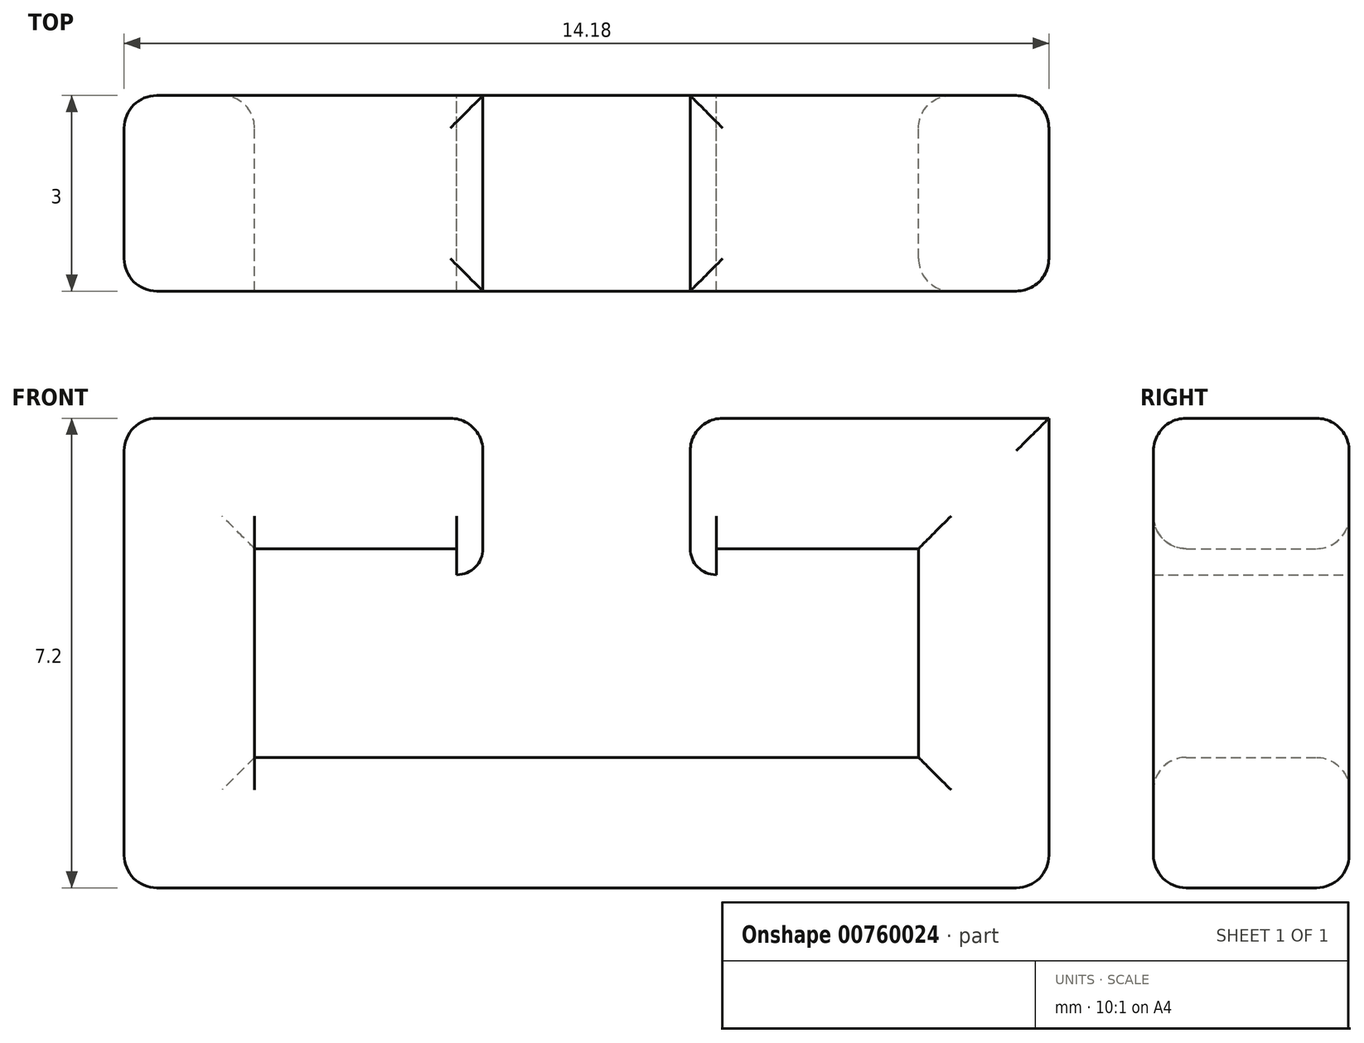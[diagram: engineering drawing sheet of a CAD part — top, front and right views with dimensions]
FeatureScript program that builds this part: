
annotation { "Feature Type Name" : "Feature", "Feature Type Description" : "" }
export const myFeature = defineFeature(function(context is Context, id is Id, definition is map)
    precondition{}
    {
        {
            var Q0;
            Q0=qCreatedBy(makeId("Front.planeOp"),FACE);
            var sketch = newSketch(context, id + "F0", { "sketchPlane" : qUnion([Q0])});
            skLineSegment(sketch, "E0.bottom", {"start": v(-7.09, -3.6) * mm, "end": v(7.09, -3.6) * mm});
            skLineSegment(sketch, "E0.top", {"start": v(-7.09, 3.6) * mm, "end": v(-1.59, 3.6) * mm});
            skLineSegment(sketch, "E0.left", {"start": v(-7.09, -3.6) * mm, "end": v(-7.09, 3.6) * mm});
            skLineSegment(sketch, "E0.right", {"start": v(7.09, -3.6) * mm, "end": v(7.09, 3.6) * mm});
            skPoint(sketch, "E0.middle", {"position": v(0, 0) * mm});
            skLineSegment(sketch, "E1.bottom", {"start": v(5.09, 1.6) * mm, "end": v(1.99, 1.6) * mm});
            skLineSegment(sketch, "E1.top", {"start": v(5.09, -1.6) * mm, "end": v(-5.09, -1.6) * mm});
            skLineSegment(sketch, "E1.left", {"start": v(5.09, 1.6) * mm, "end": v(5.09, -1.6) * mm});
            skLineSegment(sketch, "E1.right", {"start": v(-5.09, 1.6) * mm, "end": v(-5.09, -1.6) * mm});
            skLineSegment(sketch, "E2.top", {"start": v(1.59, 1.2) * mm, "end": v(1.99, 1.2) * mm});
            skLineSegment(sketch, "E2.left", {"start": v(1.59, 1.6) * mm, "end": v(1.59, 1.2) * mm});
            skLineSegment(sketch, "E2.right", {"start": v(1.99, 1.6) * mm, "end": v(1.99, 1.2) * mm});
            skLineSegment(sketch, "E3", {"start": v(-1.59, 1.6) * mm, "end": v(-1.59, 3.6) * mm});
            skLineSegment(sketch, "E4", {"start": v(1.59, 1.6) * mm, "end": v(1.59, 3.6) * mm});
            skLineSegment(sketch, "E5.trimOffspring", {"start": v(1.59, 3.6) * mm, "end": v(7.09, 3.6) * mm});
            skLineSegment(sketch, "E6.trimOffspring", {"start": v(-1.99, 1.6) * mm, "end": v(-5.09, 1.6) * mm});
            skLineSegment(sketch, "E7.top", {"start": v(-1.59, 1.2) * mm, "end": v(-1.99, 1.2) * mm});
            skLineSegment(sketch, "E7.left", {"start": v(-1.59, 1.6) * mm, "end": v(-1.59, 1.2) * mm});
            skLineSegment(sketch, "E7.right", {"start": v(-1.99, 1.6) * mm, "end": v(-1.99, 1.2) * mm});
            skSolve(sketch);
        }
        {
            var Q0;
            Q0=makeQuery(id+"F0.imprint","IMPRINT",FACE,{"disambiguationData":[TD([[makeQuery(id+"F0.imprint","IMPRINT",EDGE,{"derivedFrom":sQuery(id+"F0.wireOp",EDGE,"E0.bottom")}),1.0]])]});
            extrude(context, id + "F1", {"entities" : qUnion([Q0]), "depth" : 3 * mm, "offsetDistance" : 25 * mm});
        }
        {
            var Q0;
            Q0=makeQuery(id+"F1.opExtrude","CAP_EDGE",EDGE,{"disambiguationData":[OSD([sQuery(id+"F0.wireOp",EDGE,"E5.trimOffspring")])],"isStart":true});
            var Q1;
            Q1=makeQuery(id+"F1.opExtrude","CAP_EDGE",EDGE,{"disambiguationData":[OSD([sQuery(id+"F0.wireOp",EDGE,"E0.top")])],"isStart":true});
            var Q2;
            Q2=makeQuery(id+"F1.opExtrude","CAP_EDGE",EDGE,{"disambiguationData":[OSD([sQuery(id+"F0.wireOp",EDGE,"E0.left")])],"isStart":true});
            var Q3;
            Q3=makeQuery(id+"F1.opExtrude","CAP_EDGE",EDGE,{"disambiguationData":[OSD([sQuery(id+"F0.wireOp",EDGE,"E0.bottom")])],"isStart":true});
            var Q4;
            Q4=makeQuery(id+"F1.opExtrude","CAP_EDGE",EDGE,{"disambiguationData":[OSD([sQuery(id+"F0.wireOp",EDGE,"E0.right")])],"isStart":true});
            var Q5;
            Q5=makeQuery(id+"F1.opExtrude","SWEPT_EDGE",EDGE,{"disambiguationData":[OSD([sQuery(id+"F0.wireOp",EDGE,"E4"),sQuery(id+"F0.wireOp",EDGE,"E5.trimOffspring")])]});
            var Q6;
            Q6=makeQuery(id+"F1.opExtrude","SWEPT_EDGE",EDGE,{"disambiguationData":[OSD([sQuery(id+"F0.wireOp",EDGE,"E0.top"),sQuery(id+"F0.wireOp",EDGE,"E3")])]});
            var Q7;
            Q7=makeQuery(id+"F1.opExtrude","CAP_EDGE",EDGE,{"disambiguationData":[OSD([sQuery(id+"F0.wireOp",EDGE,"E0.top")])],"isStart":false});
            var Q8;
            Q8=makeQuery(id+"F1.opExtrude","SWEPT_EDGE",EDGE,{"disambiguationData":[OSD([sQuery(id+"F0.wireOp",EDGE,"E0.top"),sQuery(id+"F0.wireOp",EDGE,"E0.left")])]});
            var Q9;
            Q9=makeQuery(id+"F1.opExtrude","CAP_EDGE",EDGE,{"disambiguationData":[OSD([sQuery(id+"F0.wireOp",EDGE,"E5.trimOffspring")])],"isStart":false});
            var Q10;
            Q10=makeQuery(id+"F1.opExtrude","CAP_EDGE",EDGE,{"disambiguationData":[OSD([sQuery(id+"F0.wireOp",EDGE,"E1.bottom")])],"isStart":false});
            var Q11;
            Q11=makeQuery(id+"F1.opExtrude","CAP_EDGE",EDGE,{"disambiguationData":[OSD([sQuery(id+"F0.wireOp",EDGE,"E6.trimOffspring")])],"isStart":false});
            var Q12;
            Q12=makeQuery(id+"F1.opExtrude","CAP_EDGE",EDGE,{"disambiguationData":[OSD([sQuery(id+"F0.wireOp",EDGE,"E1.bottom")])],"isStart":true});
            var Q13;
            Q13=makeQuery(id+"F1.opExtrude","CAP_EDGE",EDGE,{"disambiguationData":[OSD([sQuery(id+"F0.wireOp",EDGE,"E6.trimOffspring")])],"isStart":true});
            var Q14;
            Q14=makeQuery(id+"F1.opExtrude","CAP_EDGE",EDGE,{"disambiguationData":[OSD([sQuery(id+"F0.wireOp",EDGE,"E0.left")])],"isStart":false});
            var Q15;
            Q15=makeQuery(id+"F1.opExtrude","CAP_EDGE",EDGE,{"disambiguationData":[OSD([sQuery(id+"F0.wireOp",EDGE,"E0.right")])],"isStart":false});
            var Q16;
            Q16=makeQuery(id+"F1.opExtrude","CAP_EDGE",EDGE,{"disambiguationData":[OSD([sQuery(id+"F0.wireOp",EDGE,"E1.left")])],"isStart":false});
            var Q17;
            Q17=makeQuery(id+"F1.opExtrude","CAP_EDGE",EDGE,{"disambiguationData":[OSD([sQuery(id+"F0.wireOp",EDGE,"E1.right")])],"isStart":true});
            var Q18;
            Q18=makeQuery(id+"F1.opExtrude","SWEPT_EDGE",EDGE,{"disambiguationData":[OSD([sQuery(id+"F0.wireOp",EDGE,"E0.bottom"),sQuery(id+"F0.wireOp",EDGE,"E0.left")])]});
            var Q19;
            Q19=makeQuery(id+"F1.opExtrude","SWEPT_EDGE",EDGE,{"disambiguationData":[OSD([sQuery(id+"F0.wireOp",EDGE,"E0.bottom"),sQuery(id+"F0.wireOp",EDGE,"E0.right")])]});
            var Q20;
            Q20=makeQuery(id+"F1.opExtrude","CAP_EDGE",EDGE,{"disambiguationData":[OSD([sQuery(id+"F0.wireOp",EDGE,"E1.left")])],"isStart":true});
            var Q21;
            Q21=makeQuery(id+"F1.opExtrude","CAP_EDGE",EDGE,{"disambiguationData":[OSD([sQuery(id+"F0.wireOp",EDGE,"E1.top")])],"isStart":true});
            var Q22;
            Q22=makeQuery(id+"F1.opExtrude","CAP_EDGE",EDGE,{"disambiguationData":[OSD([sQuery(id+"F0.wireOp",EDGE,"E1.top")])],"isStart":false});
            var Q23;
            Q23=makeQuery(id+"F1.opExtrude","CAP_EDGE",EDGE,{"disambiguationData":[OSD([sQuery(id+"F0.wireOp",EDGE,"E0.bottom")])],"isStart":false});
            fillet(context, id + "F2", {"entities" : qUnion([Q0, Q1, Q2, Q3, Q4, Q5, Q6, Q7, Q8, Q9, Q10, Q11, Q12, Q13, Q14, Q15, Q16, Q17, Q18, Q19, Q20, Q21, Q22, Q23]), "radius" : .5 * mm, "tangentPropagation" : true, "allowEdgeOverflow" : false});
        }
        {
            var Q0;
            Q0=makeQuery(id+"F1.opExtrude","SWEPT_EDGE",EDGE,{"disambiguationData":[OSD([sQuery(id+"F0.wireOp",EDGE,"E2.top"),sQuery(id+"F0.wireOp",EDGE,"E2.left")])]});
            var Q1;
            Q1=makeQuery(id+"F1.opExtrude","SWEPT_EDGE",EDGE,{"disambiguationData":[OSD([sQuery(id+"F0.wireOp",EDGE,"E7.top"),sQuery(id+"F0.wireOp",EDGE,"E7.left")])]});
            fillet(context, id + "F3", {"entities" : qUnion([Q0, Q1]), "radius" : .4 * mm, "tangentPropagation" : true, "allowEdgeOverflow" : false});
        }
    });
